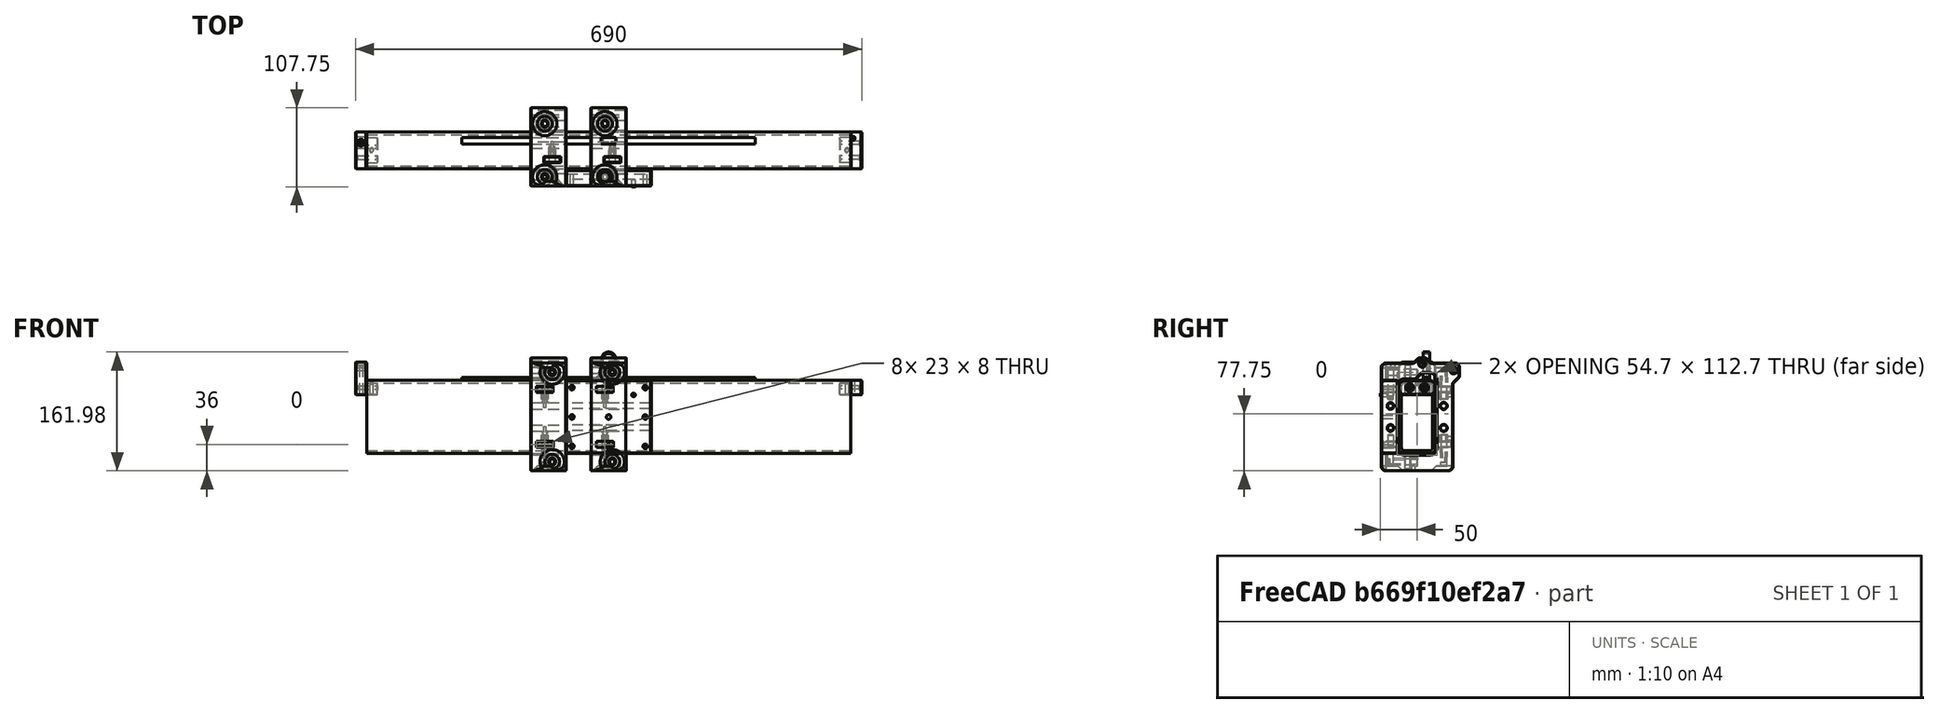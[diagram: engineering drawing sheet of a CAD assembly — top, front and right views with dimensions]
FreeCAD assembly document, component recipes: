
FREECAD ASSEMBLY — COMPONENT RECIPES ("Fabricatable-Axis-6.0")

This assembly document has 12 components, labeled P0..P11 below (a component is one placed body or linked part). 11 of them carry a construction recipe — the FreeCAD feature program that regenerates the part from scratch, quoted from this document or its linked companion documents; the rest are supplied as boundary geometry only. No exploded tour is included for this assembly.
COMPONENT P0 — recipe-attached ("Body - hole maker non adjustable", modeled in this document).
Construction recipe (the document's own serialized feature program — sketch geometry with constraints, then the solid features built on it; lengths are millimeters unless a unit is written):

FEATURE [Sketcher::SketchObject] Sketch005
  ArcFitTolerance = 1e-06
  AttachmentSupport = -> [XY_Plane008]
  FullyConstrained = true
  MakeInternals = false
  MapMode = 5
  expr: Constraints[11] = -VarSet.Bearing_od / 2 - VarSet.Carriage_to_bearing_top_clearance
  expr: Constraints[31] = VarSet.Bearing_slot_width_margin + VarSet.Bearing_od + 2 mm
  expr: Constraints[32] = -VarSet.Bearing_od / 2 - VarSet.Carriage_to_bearing_top_clearance + 1 mm
  expr: Constraints[33] = -VarSet.Bearing_od / 2 - VarSet.Carriage_to_bearing_top_clearance + 3 mm
  expr: Constraints[8] = VarSet.Bearing_slot_width_margin + VarSet.Bearing_od
  expr: Constraints[9] = VarSet.Bearing_od / 2
  sketch-geometry (13):
    g0: LineSegment StartX=11.5 StartY=-12.5 StartZ=0 EndX=11.5 EndY=11 EndZ=0
    g1: LineSegment StartX=11.5 StartY=11 StartZ=0 EndX=-11.5 EndY=11 EndZ=0
    g2: LineSegment StartX=-11.5 StartY=11 StartZ=0 EndX=-11.5 EndY=-12.5 EndZ=0
    g3: LineSegment StartX=-11.5 StartY=-12.5 StartZ=0 EndX=11.5 EndY=-12.5 EndZ=0
    g4: GeomPoint [constr] X=0 Y=0 Z=0
    g5: LineSegment StartX=11.5 StartY=-11.5 StartZ=0 EndX=12.5 EndY=-11.5 EndZ=0
    g6: LineSegment StartX=12.5 StartY=-11.5 StartZ=0 EndX=12.5 EndY=-9.5 EndZ=0
    g7: LineSegment StartX=12.5 StartY=-9.5 StartZ=0 EndX=11.5 EndY=-9.5 EndZ=0
    g8: LineSegment StartX=11.5 StartY=-9.5 StartZ=0 EndX=11.5 EndY=-11.5 EndZ=0
    g9: LineSegment StartX=-11.5 StartY=-9.5 StartZ=0 EndX=-12.5 EndY=-9.5 EndZ=0
    g10: LineSegment StartX=-12.5 StartY=-9.5 StartZ=0 EndX=-12.5 EndY=-11.5 EndZ=0
    g11: LineSegment StartX=-12.5 StartY=-11.5 StartZ=0 EndX=-11.5 EndY=-11.5 EndZ=0
    g12: LineSegment StartX=-11.5 StartY=-11.5 StartZ=0 EndX=-11.5 EndY=-9.5 EndZ=0
  constraints (34):
    c: Coincident(g0,g1)
    c: Coincident(g1,g2)
    c: Coincident(g2,g3)
    c: Coincident(g3,g0)
    c: Vertical(g0)
    c: Vertical(g2)
    c: Horizontal(g1)
    c: Coincident(g4,g-1)
    c: Distance(g3) = 23
    c: DistanceY(g-1,g0) = 11
    c: Symmetric(g0,g2,g-2)
    c: DistanceY(g-1,g0) = -12.5
    c: Coincident(g5,g6)
    c: Coincident(g6,g7)
    c: Coincident(g7,g8)
    c: Coincident(g8,g5)
    c: Horizontal(g5)
    c: Horizontal(g7)
    c: Vertical(g6)
    c: Vertical(g8)
    c: PointOnObject(g5,g0)
    c: Coincident(g9,g10)
    c: Coincident(g10,g11)
    c: Coincident(g11,g12)
    c: Coincident(g12,g9)
    c: Horizontal(g9)
    c: Horizontal(g11)
    c: Vertical(g10)
    c: Vertical(g12)
    c: Symmetric(g9,g7,g-2)
    c: Symmetric(g10,g5,g-2)
    c: Distance(g5,g10) = 25
    c: DistanceY(g-1,g5) = -11.5
    c: DistanceY(g-1,g6) = -9.5
FEATURE [PartDesign::Pad] Pad004
  Direction = (0,0,1)
  Length = 8
  Length2 = 10
  Midplane = true
  Profile = -> Sketch005
  ReferenceAxis = -> Sketch005 [N_Axis]
  Refine = true
  Suppressed = false
  Type = 0
  expr: Length = VarSet.Bearing_width + VarSet.Bearing_slot_width_margin
FEATURE [Sketcher::SketchObject] Sketch007
  ArcFitTolerance = 1e-06
  AttachmentOffset = pos=(0,0,4) rot=(0,0,1;0rad)
  AttachmentSupport = -> [XY_Plane008]
  FullyConstrained = true
  MakeInternals = false
  MapMode = 5
  Placement = pos=(0,0,4) rot=(0,0,1;0rad)
  expr: .AttachmentOffset.Base.z = Pad004.Length / 2
  expr: Constraints[1] = VarSet.Bearing_od / 1.8
  sketch-geometry (1):
    g0: Circle CenterX=0 CenterY=0 CenterZ=0 NormalX=0 NormalY=0 NormalZ=1 AngleXU=0 Radius=6.11111
  constraints (2):
    c: Coincident(g0,g-1)
    c: Diameter(g0) = 12.2222
FEATURE [PartDesign::Pocket] Pocket001
  BaseFeature = -> Pad004
  Direction = (0,0,-1)
  Length = 0.36
  Length2 = 5
  Profile = -> Sketch007
  ReferenceAxis = -> Sketch007 [N_Axis]
  Refine = true
  Suppressed = false
  Type = 0
  expr: Length = VarSet.Bearing_washer_protrusion
FEATURE [PartDesign::LinearPattern] LinearPattern
  BaseFeature = -> Pocket001
  Direction = -> Z_Axis008
  Length = 7.64
  Mode = 0
  Occurrences = 2
  Offset = 7.64
  Originals = -> [Pocket001]
  Refine = true
  Reversed = true
  Suppressed = false
  TransformMode = 0
  expr: Length = Pad004.Length - Pocket001.Length
FEATURE [Sketcher::SketchObject] Sketch008
  ArcFitTolerance = 1e-06
  AttachmentSupport = -> [XY_Plane008]
  FullyConstrained = true
  MakeInternals = false
  MapMode = 5
  expr: Constraints[1] = VarSet.Bearing_axle_screw_selftap_diameter
  sketch-geometry (1):
    g0: Circle CenterX=0 CenterY=0 CenterZ=0 NormalX=0 NormalY=0 NormalZ=1 AngleXU=0 Radius=3.85
  constraints (2):
    c: Coincident(g0,g-1)
    c: Diameter(g0) = 7.7
FEATURE [PartDesign::Pad] Pad005
  BaseFeature = -> LinearPattern
  Direction = (0,0,1)
  Length = 29.5
  Length2 = 10
  Profile = -> Sketch008
  ReferenceAxis = -> Sketch008 [N_Axis]
  Refine = true
  Suppressed = false
  Type = 0
  expr: Length = VarSet.Bearing_width / 2 + VarSet.Bearing_distance_from_fillet + VarSet.Tube_fillet_radius + VarSet.Bearing_od + VarSet.Carriage_to_bearing_top_clearance - VarSet.Bearing_axle_screw_head_pocket_depth
FEATURE [PartDesign::Pad] Pad006
  BaseFeature = -> Pad005
  Direction = (0,0,1)
  Length = 13.5
  Length2 = 10
  Profile = -> Sketch008
  ReferenceAxis = -> Sketch008 [N_Axis]
  Refine = true
  Reversed = true
  Suppressed = false
  Type = 0
  expr: Length = VarSet.Bearing_axle_screw_length + 3 mm - Pad005.Length
FEATURE [Sketcher::SketchObject] Sketch009
  ArcFitTolerance = 1e-06
  AttachmentSupport = -> [Pad006]
  FullyConstrained = true
  MakeInternals = false
  MapMode = 5
  Placement = pos=(0,0,29.5) rot=(0,0,1;0rad)
  expr: Constraints[1] = VarSet.Bearing_axle_screw_head_pocket_diamter
  sketch-geometry (1):
    g0: Circle CenterX=0 CenterY=0 CenterZ=0 NormalX=0 NormalY=0 NormalZ=1 AngleXU=0 Radius=10
  constraints (2):
    c: Coincident(g0,g-1)
    c: Diameter(g0) = 20
FEATURE [PartDesign::Pad] Pad007
  BaseFeature = -> Pad006
  Direction = (0,0,1)
  Length = 6.5
  Length2 = 10
  Profile = -> Sketch009
  ReferenceAxis = -> Sketch009 [N_Axis]
  Refine = true
  Suppressed = false
  TaperAngle = 45
  Type = 0
  expr: Length = VarSet.Bearing_axle_screw_head_pocket_depth
FEATURE [PartDesign::Chamfer] Chamfer002
  Angle = 45
  Base = -> Pad007 [Edge46,Edge48]
  BaseFeature = -> Pad007
  ChamferType = 0
  FlipDirection = false
  Refine = true
  Size = 0.8
  Size2 = 1
  SupportTransform = false
  Suppressed = false
  UseAllEdges = false
FEATURE [PartDesign::Chamfer] Chamfer003
  Angle = 45
  Base = -> Chamfer002 [Edge51,Edge3]
  BaseFeature = -> Chamfer002
  ChamferType = 0
  FlipDirection = false
  Refine = true
  Size = 0.3
  Size2 = 1
  SupportTransform = false
  Suppressed = false
  UseAllEdges = false
FEATURE [PartDesign::Body] Body004  label="Body - hole maker non adjustable"
  AllowCompound = false
  Group = -> [Sketch005,Pad004,Sketch007,Pocket001,LinearPattern,Sketch008,Pad005,Pad006,Sketch009,Pad007,Chamfer002,Chamfer003]
  Origin = -> Origin008
  Tip = -> Chamfer003
COMPONENT P1 — recipe-attached ("Body for boolean - hole maker adjustable", modeled in this document).
Construction recipe (the document's own serialized feature program — sketch geometry with constraints, then the solid features built on it; lengths are millimeters unless a unit is written):

FEATURE [PartDesign::FeatureBase] Clone007
  BaseFeature = -> LinearPattern
  Suppressed = false
FEATURE [PartDesign::Body] Body005  label="Body for boolean - hole maker adjustable"
  AllowCompound = false
  Group = -> [Clone007]
  Origin = -> Origin009
  Tip = -> Clone007
COMPONENT P2 — recipe-attached ("Body for boolean - rotation hole", modeled in this document).
Construction recipe (the document's own serialized feature program — sketch geometry with constraints, then the solid features built on it; lengths are millimeters unless a unit is written):

FEATURE [Sketcher::SketchObject] Sketch013
  ArcFitTolerance = 1e-06
  AttachmentSupport = -> [YZ_Plane011]
  FullyConstrained = true
  MakeInternals = false
  MapMode = 5
  Placement = pos=(0,0,0) rot=(0.57735,0.57735,0.57735;2.0944rad)
  expr: .Constraints.z = Pad005.Length - VarSet.Bearing_axel_screw_oval_hole_depth
  expr: Constraints[12] = VarSet.Bearing_axle_screw_diameter_loose_diamter + VarSet.Tuning_range_bearing
  expr: Constraints[7] = -Pad006.Length
  expr: Constraints[8] = VarSet.Bearing_axle_screw_diameter_loose_diamter
  sketch-geometry (5):
    g0: LineSegment StartX=-4.25 StartY=24.5 StartZ=0 EndX=-5.80102 EndY=-13.5 EndZ=0
    g1: LineSegment StartX=-5.80102 StartY=-13.5 StartZ=0 EndX=5.80102 EndY=-13.5 EndZ=0
    g2: LineSegment StartX=5.80102 StartY=-13.5 StartZ=0 EndX=4.25 EndY=24.5 EndZ=0
    g3: LineSegment StartX=4.25 StartY=24.5 StartZ=0 EndX=-4.25 EndY=24.5 EndZ=0
    g4: LineSegment [constr] StartX=-5.25 StartY=0 StartZ=0 EndX=5.25 EndY=0 EndZ=0
  constraints (14):
    c: Coincident(g0,g1)
    c: Coincident(g1,g2)
    c: Coincident(g2,g3)
    c: Coincident(g3,g0)
    c: Symmetric(g2,g0,g-2)
    c: Symmetric(g0,g1,g-2)
    c: DistanceY(g-1,g2) = 24.5  'z'
    c: DistanceY(g-1,g1) = -13.5
    c: Distance(g3) = 8.5
    c: Distance(g1) = 11.602
    c: PointOnObject(g4,g-1)
    c: Symmetric(g4,g4,g-2)
    c: Distance(g4) = 10.5
    c: PointOnObject(g4,g0)
FEATURE [PartDesign::Pad] Pad008
  Direction = (1,0,0)
  Length = 8.5
  Length2 = 10
  Midplane = true
  Placement = pos=(0,0,0) rot=(1,1,1;2.0944rad)
  Profile = -> Sketch013
  ReferenceAxis = -> Sketch013 [N_Axis]
  Refine = true
  Suppressed = false
  Type = 0
  expr: Length = VarSet.Bearing_axle_screw_diameter_loose_diamter
FEATURE [PartDesign::Chamfer] Chamfer004
  Angle = 45
  Base = -> Pad008 [Edge4,Edge3,Edge10,Edge9]
  BaseFeature = -> Pad008
  ChamferType = 0
  FlipDirection = false
  Placement = pos=(0,0,0) rot=(1,1,1;2.0944rad)
  Refine = true
  Size = 2.42857
  Size2 = 1
  SupportTransform = false
  Suppressed = false
  UseAllEdges = false
  expr: Size = VarSet.Bearing_axle_screw_diameter_loose_diamter / 3.5
FEATURE [PartDesign::Chamfer] Chamfer005
  Angle = 45
  Base = -> Chamfer004 [Face5]
  BaseFeature = -> Chamfer004
  ChamferType = 0
  FlipDirection = false
  Placement = pos=(0,0,0) rot=(1,1,1;2.0944rad)
  Refine = true
  Size = 0.8
  Size2 = 1
  SupportTransform = false
  Suppressed = false
  UseAllEdges = false
FEATURE [Sketcher::SketchObject] Sketch014
  ArcFitTolerance = 1e-06
  AttachmentOffset = pos=(0,0,24.5) rot=(0,0,1;0rad)
  AttachmentSupport = -> [XY_Plane011]
  FullyConstrained = false
  MakeInternals = false
  MapMode = 5
  Placement = pos=(0,0,24.5) rot=(0,0,1;0rad)
  expr: .AttachmentOffset.Base.z = Sketch013.Constraints.z
  expr: Constraints[5] = VarSet.Bearing_axle_screw_diameter
  expr: Constraints[6] = VarSet.Bearing_axle_screw_diameter_oval_selftap_diameter
  sketch-geometry (5):
    g0: Ellipse CenterX=0 CenterY=0 CenterZ=0 NormalX=0 NormalY=0 NormalZ=1 MajorRadius=4 MinorRadius=3.75 AngleXU=-1.5708
    g1: LineSegment [constr] StartX=1e-16 StartY=-4 StartZ=0 EndX=-1e-16 EndY=4 EndZ=0
    g2: LineSegment [constr] StartX=3.75 StartY=1e-16 StartZ=0 EndX=-3.75 EndY=-1e-16 EndZ=0
    g3: GeomPoint [constr] X=2e-16 Y=-1.39194 Z=0
    g4: GeomPoint [constr] X=0 Y=1.39194 Z=0
  constraints (4):
    c: InternalAlignment(g1-g4 -> g0) x4
    c: Coincident(g0,g-1)
    c: Distance(g1,g1) = 8
    c: Distance(g2,g2) = 7.5
FEATURE [PartDesign::Pad] Pad009
  BaseFeature = -> Chamfer005
  Direction = (0,0,1)
  Length = 5
  Length2 = 10
  Placement = pos=(0,0,0) rot=(1,1,1;2.0944rad)
  Profile = -> Sketch014
  ReferenceAxis = -> Sketch014 [N_Axis]
  Refine = true
  Suppressed = false
  Type = 0
  expr: Length = VarSet.Bearing_axel_screw_oval_hole_depth
FEATURE [Sketcher::SketchObject] Sketch015
  ArcFitTolerance = 1e-06
  AttachmentOffset = pos=(0,0,29.5) rot=(0,0,1;0rad)
  AttachmentSupport = -> [XY_Plane011]
  FullyConstrained = true
  MakeInternals = false
  MapMode = 5
  Placement = pos=(0,0,29.5) rot=(0,0,1;0rad)
  expr: .AttachmentOffset.Base.z = Sketch013.Constraints.z + VarSet.Bearing_axel_screw_oval_hole_depth
  expr: Constraints[1] = VarSet.Bearing_axle_screw_head_pocket_diamter
  sketch-geometry (1):
    g0: Circle CenterX=0 CenterY=0 CenterZ=0 NormalX=0 NormalY=0 NormalZ=1 AngleXU=0 Radius=10
  constraints (2):
    c: Coincident(g0,g-1)
    c: Diameter(g0) = 20
FEATURE [PartDesign::Pad] Pad010
  BaseFeature = -> Pad009
  Direction = (0,0,1)
  Length = 32.5
  Length2 = 10
  Placement = pos=(0,0,0) rot=(1,1,1;2.0944rad)
  Profile = -> Sketch015
  ReferenceAxis = -> Sketch015 [N_Axis]
  Refine = true
  Suppressed = false
  TaperAngle = 45
  Type = 0
  expr: Length = VarSet.Bearing_axle_screw_head_pocket_depth * 5
FEATURE [Sketcher::SketchObject] Sketch016
  ArcFitTolerance = 1e-06
  AttachmentSupport = -> [XZ_Plane011]
  FullyConstrained = true
  MakeInternals = false
  MapMode = 5
  Placement = pos=(0,0,0) rot=(1,0,0;1.5708rad)
  expr: .Constraints.z = -VarSet.Bearing_width / 2 - VarSet.Bearing_slot_width_margin / 2 - VarSet.Bearing_tuning_screw_selftap_diameter / 2 - 1.8 mm
  expr: Constraints[1] = VarSet.Bearing_tuning_screw_selftap_diameter
  sketch-geometry (1):
    g0: Circle CenterX=0 CenterY=-8.1 CenterZ=0 NormalX=0 NormalY=0 NormalZ=1 AngleXU=0 Radius=2.3
  constraints (3):
    c: PointOnObject(g0,g-2)
    c: Diameter(g0) = 4.6
    c: DistanceY(g-1,g0) = -8.1  'z'
FEATURE [PartDesign::Pad] Pad011
  BaseFeature = -> Pad010
  Direction = (0,-1,2e-16)
  Length = 11.5
  Length2 = 10
  Placement = pos=(0,0,0) rot=(1,1,1;2.0944rad)
  Profile = -> Sketch016
  ReferenceAxis = -> Sketch016 [N_Axis]
  Refine = true
  Suppressed = false
  Type = 0
  expr: Length = VarSet.Bearing_od / 2 + VarSet.Carriage_to_bearing_top_clearance - 1 mm
FEATURE [Sketcher::SketchObject] Sketch017
  ArcFitTolerance = 1e-06
  AttachmentOffset = pos=(0,0,11.5) rot=(0,0,1;0rad)
  AttachmentSupport = -> [XZ_Plane011]
  FullyConstrained = true
  MakeInternals = false
  MapMode = 5
  Placement = pos=(0,-11.5,2.6e-15) rot=(1,0,0;1.5708rad)
  expr: .AttachmentOffset.Base.z = VarSet.Bearing_od / 2 + VarSet.Carriage_to_bearing_top_clearance - 1 mm
  expr: Constraints[0] = VarSet.Bearing_tuning_screw_selftap_diameter
  expr: Constraints[1] = Sketch016.Constraints.z
  sketch-geometry (1):
    g0: Circle CenterX=0 CenterY=-8.1 CenterZ=0 NormalX=0 NormalY=0 NormalZ=1 AngleXU=0 Radius=2.3
  constraints (3):
    c: Diameter(g0) = 4.6
    c: DistanceY(g-1,g0) = -8.1
    c: PointOnObject(g0,g-2)
FEATURE [PartDesign::Pad] Pad012
  BaseFeature = -> Pad011
  Direction = (0,-1,2e-16)
  Length = 1
  Length2 = 10
  Placement = pos=(0,0,0) rot=(1,1,1;2.0944rad)
  Profile = -> Sketch017
  ReferenceAxis = -> Sketch017 [N_Axis]
  Refine = true
  Suppressed = false
  TaperAngle = 45
  Type = 0
FEATURE [PartDesign::Chamfer] Chamfer006
  Angle = 45
  Base = -> Pad012 [Edge44]
  BaseFeature = -> Pad012
  ChamferType = 0
  FlipDirection = false
  Placement = pos=(0,0,0) rot=(1,1,1;2.0944rad)
  Refine = true
  Size = 0.8
  Size2 = 1
  SupportTransform = false
  Suppressed = false
  UseAllEdges = false
FEATURE [PartDesign::Body] Body007  label="Body for boolean - rotation hole"
  AllowCompound = false
  Group = -> [Sketch013,Pad008,Chamfer004,Chamfer005,Sketch014,Pad009,Sketch015,Pad010,Sketch016,Pad011,Sketch017,Pad012,Chamfer006]
  Origin = -> Origin011
  Tip = -> Chamfer006
COMPONENT P3 — recipe-attached ("Belt", modeled in this document).
Construction recipe (the document's own serialized feature program — sketch geometry with constraints, then the solid features built on it; lengths are millimeters unless a unit is written):

FEATURE [Sketcher::SketchObject] Sketch018
  ArcFitTolerance = 1e-06
  AttachmentSupport = -> [XZ_Plane012]
  FullyConstrained = false
  MakeInternals = false
  MapMode = 5
  Placement = pos=(0,0,0) rot=(1,0,0;1.5708rad)
  expr: Constraints[31] = 16
  sketch-geometry (16):
    g0: LineSegment StartX=-200 StartY=0 StartZ=0 EndX=-21 EndY=0 EndZ=0
    g1: LineSegment StartX=21 StartY=0 StartZ=0 EndX=200 EndY=0 EndZ=0
    g2: ArcOfCircle CenterX=-1e-16 CenterY=26.9798 CenterZ=0 NormalX=0 NormalY=0 NormalZ=1 AngleXU=0 Radius=8 StartAngle=1e-16 EndAngle=3.14159
    g3: ArcOfCircle CenterX=-1e-16 CenterY=26.9798 CenterZ=0 NormalX=0 NormalY=0 NormalZ=1 AngleXU=0 Radius=10 StartAngle=0 EndAngle=3.14159
    g4: ArcOfCircle CenterX=-21 CenterY=13 CenterZ=0 NormalX=0 NormalY=0 NormalZ=1 AngleXU=0 Radius=13 StartAngle=4.71239 EndAngle=6.28319
    g5: ArcOfCircle CenterX=21 CenterY=13 CenterZ=0 NormalX=0 NormalY=0 NormalZ=1 AngleXU=0 Radius=13 StartAngle=3.14159 EndAngle=4.71239
    g6: ArcOfCircle CenterX=21 CenterY=13 CenterZ=0 NormalX=0 NormalY=0 NormalZ=1 AngleXU=0 Radius=11 StartAngle=3.14159 EndAngle=4.71239
    g7: ArcOfCircle CenterX=-21 CenterY=13 CenterZ=0 NormalX=0 NormalY=0 NormalZ=1 AngleXU=0 Radius=11 StartAngle=4.71239 EndAngle=6.28319
    g8: LineSegment StartX=-200 StartY=0 StartZ=0 EndX=-200 EndY=2 EndZ=0
    g9: LineSegment StartX=-200 StartY=2 StartZ=0 EndX=-21 EndY=2 EndZ=0
    g10: LineSegment StartX=200 StartY=0 StartZ=0 EndX=200 EndY=2 EndZ=0
    g11: LineSegment StartX=200 StartY=2 StartZ=0 EndX=21 EndY=2 EndZ=0
    g12: LineSegment StartX=-10 StartY=26.9798 StartZ=0 EndX=-10 EndY=13 EndZ=0
    g13: LineSegment StartX=-8 StartY=26.9798 StartZ=0 EndX=-8 EndY=13 EndZ=0
    g14: LineSegment StartX=8 StartY=26.9798 StartZ=0 EndX=8 EndY=13 EndZ=0
    g15: LineSegment StartX=10 StartY=26.9798 StartZ=0 EndX=10 EndY=13 EndZ=0
  constraints (36):
    c: PointOnObject(g0,g-1)
    c: PointOnObject(g0,g-1)
    c: PointOnObject(g1,g-1)
    c: Coincident(g3,g2)
    c: Coincident(g6,g5)
    c: Coincident(g7,g4)
    c: Coincident(g0,g8)
    c: Vertical(g8)
    c: Coincident(g8,g9)
    c: Horizontal(g9)
    c: Coincident(g1,g10)
    c: Vertical(g10)
    c: Coincident(g10,g11)
    c: Horizontal(g11)
    c: Tangent(g1,g5) = -1.5708
    c: Tangent(g6,g11) = 1.5708
    c: Tangent(g5,g14) = -1.5708
    c: Tangent(g15,g6) = -1.5708
    c: Tangent(g15,g3) = 1.5708
    c: Tangent(g14,g2) = 1.5708
    c: Tangent(g4,g0) = -1.5708
    c: Tangent(g7,g9) = -1.5708
    c: Tangent(g7,g12) = 1.5708
    c: Tangent(g4,g13) = 1.5708
    c: Tangent(g13,g2) = -1.5708
    c: Tangent(g12,g3) = -1.5708
    c: Parallel(g12,g13)
    c: Parallel(g14,g15)
    c: Symmetric(g2,g2,g-2)
    c: Vertical(g12)
    c: Distance(g8) = 2
    c: Diameter(g2) = 16
    c: Equal(g7,g6)
    c: Diameter(g7) = 22
    c: Symmetric(g0,g1,g-2)
    c: Distance(g0,g1) = 400
FEATURE [PartDesign::Pad] Pad013
  Direction = (0,-1,2e-16)
  Length = 9
  Length2 = 10
  Placement = pos=(0,0,0) rot=(1,0,0;1.5708rad)
  Profile = -> Sketch018
  ReferenceAxis = -> Sketch018 [N_Axis]
  Refine = true
  Suppressed = false
  Type = 0
FEATURE [PartDesign::Body] Body008  label="Belt"
  AllowCompound = false
  Group = -> [Sketch018,Pad013]
  Origin = -> Origin012
  Placement = pos=(0,17.25,51.5) rot=(0,0,1;0rad)
  Tip = -> Pad013
  expr: .Placement.Base.y = VarSet.Tube_width / 2 - VarSet.Tube_fillet_radius
  expr: .Placement.Base.z = VarSet.Tube_height / 2 + 1.5 mm
COMPONENT P4 — recipe-attached ("Tuning arrow", modeled in this document).
Construction recipe (the document's own serialized feature program — sketch geometry with constraints, then the solid features built on it; lengths are millimeters unless a unit is written):

FEATURE [Sketcher::SketchObject] Sketch019
  ArcFitTolerance = 1e-06
  AttachmentOffset = pos=(0,-12.7,12.5) rot=(0,0,1;0rad)
  AttachmentSupport = -> [XZ_Plane013]
  FullyConstrained = true
  MakeInternals = false
  MapMode = 5
  Placement = pos=(0,-12.5,-12.7) rot=(1,0,0;1.5708rad)
  expr: .AttachmentOffset.Base.y = Sketch016.Constraints.z - VarSet.Bearing_tuning_screw_selftap_diameter
  expr: .AttachmentOffset.Base.z = VarSet.Bearing_od / 2 + VarSet.Carriage_to_bearing_top_clearance
  sketch-geometry (10):
    g0: LineSegment StartX=-1.25 StartY=-12 StartZ=0 EndX=1.25 EndY=-12 EndZ=0
    g1: LineSegment StartX=1.25 StartY=-12 StartZ=0 EndX=1.25 EndY=-3.82843 EndZ=0
    g2: LineSegment StartX=1.25 StartY=-3.82843 StartZ=0 EndX=3.5 EndY=-6.07843 EndZ=0
    g3: LineSegment StartX=3.5 StartY=-6.07843 StartZ=0 EndX=3.5 EndY=-3.25 EndZ=0
    g4: LineSegment StartX=3.5 StartY=-3.25 StartZ=0 EndX=0.25 EndY=-4e-16 EndZ=0
    g5: LineSegment StartX=0.25 StartY=-4e-16 StartZ=0 EndX=-0.25 EndY=0 EndZ=0
    g6: LineSegment StartX=-0.25 StartY=0 StartZ=0 EndX=-3.5 EndY=-3.25 EndZ=0
    g7: LineSegment StartX=-3.5 StartY=-3.25 StartZ=0 EndX=-3.5 EndY=-6.07843 EndZ=0
    g8: LineSegment StartX=-3.5 StartY=-6.07843 StartZ=0 EndX=-1.25 EndY=-3.82843 EndZ=0
    g9: LineSegment StartX=-1.25 StartY=-3.82843 StartZ=0 EndX=-1.25 EndY=-12 EndZ=0
  constraints (26):
    c: Horizontal(g0)
    c: Coincident(g0,g1)
    c: Vertical(g1)
    c: Coincident(g1,g2)
    c: Coincident(g2,g3)
    c: Vertical(g3)
    c: Coincident(g3,g4)
    c: Coincident(g4,g5)
    c: Coincident(g5,g6)
    c: Coincident(g6,g7)
    c: Coincident(g7,g8)
    c: Coincident(g8,g9)
    c: Coincident(g9,g0)
    c: Vertical(g9)
    c: Symmetric(g5,g4,g-2)
    c: Symmetric(g6,g3,g-2)
    c: Symmetric(g8,g1,g-2)
    c: Symmetric(g7,g2,g-2)
    c: Distance(g5) = 0.5
    c: Parallel(g8,g6)
    c: Distance(g8,g6) = 2
    c: Distance(g0) = 2.5
    c: Angle(g8,g9) = 0.785398
    c: Distance(g7,g2) = 7
    c: PointOnObject(g4,g-1)
    c: DistanceY(g-1,g0) = -12
FEATURE [PartDesign::Pad] Pad014
  Direction = (0,-1,2e-16)
  Length = 0.5
  Length2 = 10
  Placement = pos=(0,0,0) rot=(1,0,0;1.5708rad)
  Profile = -> Sketch019
  ReferenceAxis = -> Sketch019 [N_Axis]
  Refine = true
  Reversed = true
  Suppressed = false
  Type = 0
FEATURE [PartDesign::Body] Body009  label="Tuning arrow"
  AllowCompound = false
  Group = -> [Sketch019,Pad014]
  Origin = -> Origin013
  Tip = -> Pad014
COMPONENT P5 — recipe-attached ("Connector for bearing rings", modeled in this document).
Construction recipe (the document's own serialized feature program — sketch geometry with constraints, then the solid features built on it; lengths are millimeters unless a unit is written):

FEATURE [Sketcher::SketchObject] Sketch023
  ArcFitTolerance = 1e-06
  AttachmentSupport = -> [YZ_Plane016]
  FullyConstrained = true
  MakeInternals = false
  MapMode = 5
  Placement = pos=(0,0,0) rot=(0.57735,0.57735,0.57735;2.0944rad)
  expr: Constraints[10] = -VarSet.Tube_width / 2 - VarSet.Carriage_to_tube_clearance
  expr: Constraints[12] = Sketch022.Constraints.holespacing
  expr: Constraints[13] = -Sketch022.Constraints.holelocation
  expr: Constraints[15] = VarSet.Bearing_axle_screw_selftap_diameter
  expr: Constraints[8] = VarSet.Tube_height
  expr: Constraints[9] = -VarSet.Tube_width / 2 - VarSet.Bearing_od - VarSet.Carriage_to_bearing_top_clearance
  sketch-geometry (6):
    g0: LineSegment StartX=-48.75 StartY=50 StartZ=0 EndX=-48.75 EndY=-50 EndZ=0
    g1: LineSegment StartX=-48.75 StartY=-50 StartZ=0 EndX=-26.75 EndY=-50 EndZ=0
    g2: LineSegment StartX=-26.75 StartY=-50 StartZ=0 EndX=-26.75 EndY=50 EndZ=0
    g3: LineSegment StartX=-26.75 StartY=50 StartZ=0 EndX=-48.75 EndY=50 EndZ=0
    g4: Circle CenterX=-36.25 CenterY=15 CenterZ=0 NormalX=0 NormalY=0 NormalZ=1 AngleXU=0 Radius=3.85
    g5: Circle CenterX=-36.25 CenterY=-15 CenterZ=0 NormalX=0 NormalY=0 NormalZ=1 AngleXU=0 Radius=3.85
  constraints (16):
    c: Coincident(g0,g1)
    c: Coincident(g1,g2)
    c: Coincident(g2,g3)
    c: Coincident(g3,g0)
    c: Vertical(g2)
    c: Horizontal(g1)
    c: Horizontal(g3)
    c: Symmetric(g0,g0,g-1)
    c: Distance(g0) = 100
    c: DistanceX(g-2,g0) = -48.75
    c: DistanceX(g-2,g2) = -26.75
    c: Symmetric(g4,g5,g-1)
    c: Distance(g5,g4) = 30
    c: DistanceX(g-2,g4) = -36.25
    c: Equal(g5,g4)
    c: Diameter(g5) = 7.7
FEATURE [PartDesign::Pad] Pad016
  Direction = (1,0,0)
  Length = 116
  Length2 = 10
  Midplane = true
  Placement = pos=(0,0,0) rot=(1,1,1;2.0944rad)
  Profile = -> Sketch023
  ReferenceAxis = -> Sketch023 [N_Axis]
  Refine = true
  Suppressed = false
  Type = 0
  expr: Length = <<Bearing ring 1>>.Placement.Base.x * 2 - Pad002.Length
FEATURE [Sketcher::SketchObject] Sketch024
  ArcFitTolerance = 1e-06
  AttachmentSupport = -> [Pad016]
  FullyConstrained = false
  MakeInternals = false
  MapMode = 5
  Placement = pos=(-1.07e-14,-48.75,0) rot=(0.57735,0.57735,-0.57735;2.0944rad)
  sketch-geometry (9):
    g0: Circle CenterX=-40 CenterY=-50 CenterZ=0 NormalX=0 NormalY=0 NormalZ=1 AngleXU=0 Radius=3.64196
    g1: Circle CenterX=-40 CenterY=0 CenterZ=0 NormalX=0 NormalY=0 NormalZ=1 AngleXU=0 Radius=6.80044
    g2: Circle CenterX=-40 CenterY=50 CenterZ=0 NormalX=0 NormalY=0 NormalZ=1 AngleXU=0 Radius=7.67268
    g3: Circle CenterX=40 CenterY=50 CenterZ=0 NormalX=0 NormalY=0 NormalZ=1 AngleXU=0 Radius=3.2152
    g4: Circle CenterX=40 CenterY=0 CenterZ=0 NormalX=0 NormalY=0 NormalZ=1 AngleXU=0 Radius=11.4747
    g5: Circle CenterX=40 CenterY=-50 CenterZ=0 NormalX=0 NormalY=0 NormalZ=1 AngleXU=0 Radius=5.49329
    g6: Circle CenterX=0 CenterY=-50 CenterZ=0 NormalX=0 NormalY=0 NormalZ=1 AngleXU=0 Radius=9.23188
    g7: Circle CenterX=0 CenterY=0 CenterZ=0 NormalX=0 NormalY=0 NormalZ=1 AngleXU=0 Radius=8.68214
    g8: Circle CenterX=0 CenterY=50 CenterZ=0 NormalX=0 NormalY=0 NormalZ=1 AngleXU=0 Radius=6.29187
  constraints (14):
    c: PointOnObject(g1,g-1)
    c: PointOnObject(g4,g-1)
    c: PointOnObject(g6,g-2)
    c: Coincident(g7,g-1)
    c: PointOnObject(g8,g-2)
    c: Vertical(g0,g1)
    c: Vertical(g5,g4)
    c: Symmetric(g5,g3,g-1)
    c: Symmetric(g2,g0,g-1)
    c: Symmetric(g2,g3,g-2)
    c: Horizontal(g8,g3)
    c: Horizontal(g6,g5)
    c: Distance(g5,g0) = 80
    c: Distance(g0,g2) = 100
FEATURE [PartDesign::Hole] Hole
  BaseFeature = -> Pad016
  CustomThreadClearance = 0
  Depth = 316.338
  DepthType = 1
  Diameter = 4.6
  DrillForDepth = false
  DrillPoint = 1
  DrillPointAngle = 118
  HoleCutCountersinkAngle = 90
  HoleCutCustomValues = false
  HoleCutDepth = 0
  HoleCutDiameter = 6.1
  HoleCutType = 0
  ModelThread = false
  Placement = pos=(0,0,0) rot=(1,1,1;2.0944rad)
  Profile = -> Sketch024
  Refine = true
  Suppressed = false
  Tapered = false
  TaperedAngle = 90
  ThreadClass = 0
  ThreadDepth = 316.338
  ThreadDepthType = 0
  ThreadDirection = 0
  ThreadFit = 0
  ThreadSize = 0
  ThreadType = 0
  Threaded = false
  UseCustomThreadClearance = false
  expr: Diameter = VarSet.Bearing_tuning_screw_selftap_diameter
FEATURE [PartDesign::Chamfer] Chamfer009
  Angle = 45
  Base = -> Hole [Face1,Face4,Face3,Face15]
  BaseFeature = -> Hole
  ChamferType = 0
  FlipDirection = false
  Placement = pos=(0,0,0) rot=(1,1,1;2.0944rad)
  Refine = true
  Size = 0.8
  Size2 = 1
  SupportTransform = false
  Suppressed = false
  UseAllEdges = false
FEATURE [PartDesign::Body] Body012  label="Connector for bearing rings"
  AllowCompound = false
  Group = -> [Sketch023,Pad016,Sketch024,Hole,Chamfer009]
  Origin = -> Origin016
  Tip = -> Chamfer009
COMPONENT P6 — recipe-attached ("Chain lock - non-adjustable", modeled in this document).
Construction recipe (the document's own serialized feature program — sketch geometry with constraints, then the solid features built on it; lengths are millimeters unless a unit is written):

FEATURE [Sketcher::SketchObject] Sketch025
  ArcFitTolerance = 1e-06
  AttachmentSupport = -> [YZ_Plane017]
  FullyConstrained = true
  MakeInternals = false
  MapMode = 5
  Placement = pos=(0,0,0) rot=(0.57735,0.57735,0.57735;2.0944rad)
  expr: Constraints[10] = VarSet.Tube_height / 2 - 20 mm
  expr: Constraints[8] = VarSet.Tube_width
  expr: Constraints[9] = VarSet.Tube_height / 2
  sketch-geometry (4):
    g0: LineSegment StartX=-25.25 StartY=30 StartZ=0 EndX=25.25 EndY=30 EndZ=0
    g1: LineSegment StartX=25.25 StartY=30 StartZ=0 EndX=25.25 EndY=50 EndZ=0
    g2: LineSegment StartX=25.25 StartY=50 StartZ=0 EndX=-25.25 EndY=50 EndZ=0
    g3: LineSegment StartX=-25.25 StartY=50 StartZ=0 EndX=-25.25 EndY=30 EndZ=0
  constraints (11):
    c: Coincident(g0,g1)
    c: Coincident(g1,g2)
    c: Coincident(g2,g3)
    c: Coincident(g3,g0)
    c: Horizontal(g0)
    c: Vertical(g1)
    c: Vertical(g3)
    c: Symmetric(g1,g2,g-2)
    c: Distance(g2) = 50.5
    c: DistanceY(g-1,g1) = 50
    c: DistanceY(g-1,g0) = 30
FEATURE [PartDesign::Pad] Pad017
  Direction = (1,0,0)
  Length = 15
  Length2 = 10
  Placement = pos=(0,0,0) rot=(1,1,1;2.0944rad)
  Profile = -> Sketch025
  ReferenceAxis = -> Sketch025 [N_Axis]
  Refine = true
  Suppressed = false
  Type = 0
FEATURE [PartDesign::Fillet] Fillet009
  Base = -> Pad017 [Edge8,Edge1,Edge2,Edge5]
  BaseFeature = -> Pad017
  Placement = pos=(0,0,0) rot=(1,1,1;2.0944rad)
  Radius = 8
  Refine = true
  SupportTransform = false
  Suppressed = false
  UseAllEdges = false
  expr: Radius = VarSet.Tube_fillet_radius
FEATURE [Sketcher::SketchObject] Sketch026
  ArcFitTolerance = 1e-06
  AttachmentSupport = -> [YZ_Plane017]
  ExternalGeometry = -> [Fillet009]
  FullyConstrained = true
  MakeInternals = false
  MapMode = 5
  Placement = pos=(0,0,0) rot=(0.57735,0.57735,0.57735;2.0944rad)
  expr: Constraints[7] = VarSet.Tube_thickness
  sketch-geometry (4):
    g0: LineSegment StartX=-17.15 StartY=46 StartZ=0 EndX=-17.15 EndY=30 EndZ=0
    g1: LineSegment StartX=-17.15 StartY=30 StartZ=0 EndX=17.15 EndY=30 EndZ=0
    g2: LineSegment StartX=17.15 StartY=30 StartZ=0 EndX=17.15 EndY=46 EndZ=0
    g3: LineSegment StartX=17.15 StartY=46 StartZ=0 EndX=-17.15 EndY=46 EndZ=0
  constraints (11):
    c: Coincident(g0,g1)
    c: Coincident(g1,g2)
    c: Coincident(g2,g3)
    c: Coincident(g3,g0)
    c: Vertical(g0)
    c: Vertical(g2)
    c: Horizontal(g1)
    c: Distance(g0,g-4) = 4
    c: PointOnObject(g0,g-3)
    c: Distance(g0,g-3) = 0.1
    c: Symmetric(g0,g2,g-2)
FEATURE [PartDesign::Pad] Pad018
  BaseFeature = -> Fillet009
  Direction = (1,0,0)
  Length = 15
  Length2 = 10
  Placement = pos=(0,0,0) rot=(1,1,1;2.0944rad)
  Profile = -> Sketch026
  ReferenceAxis = -> Sketch026 [N_Axis]
  Refine = true
  Reversed = true
  Suppressed = false
  Type = 0
FEATURE [PartDesign::Fillet] Fillet010
  Base = -> Pad018 [Edge32,Edge29,Edge30,Edge34]
  BaseFeature = -> Pad018
  Placement = pos=(0,0,0) rot=(1,1,1;2.0944rad)
  Radius = 2
  Refine = true
  SupportTransform = false
  Suppressed = false
  UseAllEdges = false
FEATURE [Sketcher::SketchObject] Sketch027
  ArcFitTolerance = 1e-06
  AttachmentSupport = -> [XY_Plane017]
  FullyConstrained = true
  MakeInternals = false
  MapMode = 5
  expr: Constraints[0] = VarSet.Tube_width / 2 - VarSet.Tube_fillet_radius - 1 mm
  expr: Constraints[1] = 4 / 2 + 1.5
  sketch-geometry (1):
    g0: Circle CenterX=3.5 CenterY=16.25 CenterZ=0 NormalX=0 NormalY=0 NormalZ=1 AngleXU=0 Radius=1.825
  constraints (3):
    c: DistanceY(g-1,g0) = 16.25
    c: DistanceX(g-2,g0) = 3.5
    c: Diameter(g0) = 3.65
FEATURE [PartDesign::Pocket] Pocket003
  BaseFeature = -> Fillet010
  Direction = (0,0,-1)
  Length = 5
  Length2 = 5
  Midplane = true
  Placement = pos=(0,0,0) rot=(1,1,1;2.0944rad)
  Profile = -> Sketch027
  ReferenceAxis = -> Sketch027 [N_Axis]
  Refine = true
  Suppressed = false
  Type = 1
FEATURE [Sketcher::SketchObject] Sketch028
  ArcFitTolerance = 1e-06
  AttachmentSupport = -> [XY_Plane017]
  FullyConstrained = true
  MakeInternals = false
  MapMode = 5
  sketch-geometry (1):
    g0: Circle CenterX=-5 CenterY=0 CenterZ=0 NormalX=0 NormalY=0 NormalZ=1 AngleXU=0 Radius=2.3
  constraints (3):
    c: PointOnObject(g0,g-1)
    c: DistanceX(g-2,g0) = -5
    c: Diameter(g0) = 4.6
FEATURE [PartDesign::Pocket] Pocket004
  BaseFeature = -> Pocket003
  Direction = (0,0,-1)
  Length = 5
  Length2 = 5
  Placement = pos=(0,0,0) rot=(1,1,1;2.0944rad)
  Profile = -> Sketch028
  ReferenceAxis = -> Sketch028 [N_Axis]
  Refine = true
  Reversed = true
  Suppressed = false
  Type = 1
FEATURE [Sketcher::SketchObject] Sketch029
  ArcFitTolerance = 1e-06
  AttachmentSupport = -> [Pocket004]
  FullyConstrained = false
  MakeInternals = false
  MapMode = 5
  Placement = pos=(15,0,0) rot=(0.57735,0.57735,0.57735;2.0944rad)
  expr: Constraints[2] = VarSet.Tube_height / 2 - 10 mm
  sketch-geometry (2):
    g0: Circle CenterX=-10 CenterY=40 CenterZ=0 NormalX=0 NormalY=0 NormalZ=1 AngleXU=0 Radius=5.4284
    g1: Circle CenterX=10 CenterY=40 CenterZ=0 NormalX=0 NormalY=0 NormalZ=1 AngleXU=0 Radius=4.43586
  constraints (3):
    c: Symmetric(g0,g1,g-2)
    c: Distance(g1,g0) = 20
    c: DistanceY(g-1,g0) = 40
FEATURE [PartDesign::Hole] Hole001
  BaseFeature = -> Pocket004
  CustomThreadClearance = 0
  Depth = 125.342
  DepthType = 1
  Diameter = 4.6
  DrillForDepth = false
  DrillPoint = 1
  DrillPointAngle = 118
  HoleCutCountersinkAngle = 90
  HoleCutCustomValues = false
  HoleCutDepth = 0
  HoleCutDiameter = 11
  HoleCutType = 2
  ModelThread = false
  Placement = pos=(0,0,0) rot=(1,1,1;2.0944rad)
  Profile = -> Sketch029
  Refine = true
  Suppressed = false
  Tapered = false
  TaperedAngle = 90
  ThreadClass = 0
  ThreadDepth = 125.342
  ThreadDepthType = 0
  ThreadDirection = 0
  ThreadFit = 0
  ThreadSize = 0
  ThreadType = 0
  Threaded = false
  UseCustomThreadClearance = false
FEATURE [PartDesign::Chamfer] Chamfer010
  Angle = 45
  Base = -> Hole001 [Edge53,Face20,Face19,Face17,Edge17]
  BaseFeature = -> Hole001
  ChamferType = 0
  FlipDirection = false
  Placement = pos=(0,0,0) rot=(1,1,1;2.0944rad)
  Refine = true
  Size = 0.8
  Size2 = 1
  SupportTransform = false
  Suppressed = false
  UseAllEdges = false
FEATURE [PartDesign::Body] Body013  label="Chain lock - non-adjustable"
  AllowCompound = false
  Group = -> [Sketch025,Pad017,Fillet009,Sketch026,Pad018,Fillet010,Sketch027,Pocket003,Sketch028,Pocket004,Sketch029,Hole001,Chamfer010]
  Origin = -> Origin017
  Placement = pos=(330,0,0) rot=(0,0,1;0rad)
  Tip = -> Chamfer010
  expr: .Placement.Base.x = Pad.Length / 2
COMPONENT P7 — recipe-attached ("Chain lock - adjustable", modeled in this document).
Construction recipe (the document's own serialized feature program — sketch geometry with constraints, then the solid features built on it; lengths are millimeters unless a unit is written):

FEATURE [Sketcher::SketchObject] Sketch030
  ArcFitTolerance = 1e-06
  AttachmentSupport = -> [YZ_Plane018]
  FullyConstrained = true
  MakeInternals = false
  MapMode = 5
  Placement = pos=(0,0,0) rot=(0.57735,0.57735,0.57735;2.0944rad)
  expr: Constraints[11] = VarSet.Tube_width
  expr: Constraints[13] = VarSet.Tube_width / 2 - VarSet.Tube_fillet_radius - 1 mm
  expr: Constraints[7] = VarSet.Tube_height / 2 - 20 mm
  expr: Constraints[8] = VarSet.Tube_height / 2 + 15 mm
  expr: Constraints[9] = VarSet.Tube_height / 2 + 25 mm
  sketch-geometry (5):
    g0: LineSegment StartX=-25.25 StartY=75 StartZ=0 EndX=-25.25 EndY=30 EndZ=0
    g1: LineSegment StartX=-25.25 StartY=30 StartZ=0 EndX=25.25 EndY=30 EndZ=0
    g2: LineSegment StartX=25.25 StartY=30 StartZ=0 EndX=25.25 EndY=75 EndZ=0
    g3: LineSegment StartX=25.25 StartY=75 StartZ=0 EndX=-25.25 EndY=75 EndZ=0
    g4: Circle CenterX=16.25 CenterY=65 CenterZ=0 NormalX=0 NormalY=0 NormalZ=1 AngleXU=0 Radius=1.825
  constraints (14):
    c: Coincident(g0,g1)
    c: Coincident(g1,g2)
    c: Coincident(g2,g3)
    c: Coincident(g3,g0)
    c: Vertical(g0)
    c: Vertical(g2)
    c: Horizontal(g3)
    c: DistanceY(g-1,g1) = 30
    c: DistanceY(g-1,g4) = 65
    c: DistanceY(g-1,g2) = 75
    c: Symmetric(g1,g0,g-2)
    c: Distance(g3) = 50.5
    c: Diameter(g4) = 3.65
    c: DistanceX(g-2,g4) = 16.25
FEATURE [PartDesign::Pad] Pad019
  Direction = (1,0,0)
  Length = 15
  Length2 = 10
  Placement = pos=(0,0,0) rot=(1,1,1;2.0944rad)
  Profile = -> Sketch030
  ReferenceAxis = -> Sketch030 [N_Axis]
  Refine = true
  Reversed = true
  Suppressed = false
  Type = 0
FEATURE [PartDesign::Fillet] Fillet011
  Base = -> Pad019 [Edge1,Edge2,Edge5,Edge8]
  BaseFeature = -> Pad019
  Placement = pos=(0,0,0) rot=(1,1,1;2.0944rad)
  Radius = 8
  Refine = true
  SupportTransform = false
  Suppressed = false
  UseAllEdges = false
  expr: Radius = VarSet.Tube_fillet_radius
FEATURE [Sketcher::SketchObject] Sketch031
  ArcFitTolerance = 1e-06
  AttachmentSupport = -> [Fillet011]
  ExternalGeometry = -> [Fillet011]
  FullyConstrained = true
  MakeInternals = false
  MapMode = 5
  Placement = pos=(0,0,0) rot=(0.57735,0.57735,0.57735;2.0944rad)
  expr: Constraints[10] = VarSet.Tube_height / 2 - VarSet.Tube_thickness
  sketch-geometry (4):
    g0: LineSegment StartX=-17.15 StartY=30 StartZ=0 EndX=17.15 EndY=30 EndZ=0
    g1: LineSegment StartX=17.15 StartY=30 StartZ=0 EndX=17.15 EndY=46 EndZ=0
    g2: LineSegment StartX=17.15 StartY=46 StartZ=0 EndX=-17.15 EndY=46 EndZ=0
    g3: LineSegment StartX=-17.15 StartY=46 StartZ=0 EndX=-17.15 EndY=30 EndZ=0
  constraints (11):
    c: Coincident(g0,g1)
    c: Coincident(g1,g2)
    c: Coincident(g2,g3)
    c: Coincident(g3,g0)
    c: Horizontal(g2)
    c: Vertical(g1)
    c: Vertical(g3)
    c: PointOnObject(g0,g-3)
    c: Symmetric(g0,g0,g-2)
    c: Distance(g0,g-3) = 0.1
    c: DistanceY(g-1,g1) = 46
FEATURE [PartDesign::Pad] Pad020
  BaseFeature = -> Fillet011
  Direction = (1,0,0)
  Length = 15
  Length2 = 10
  Placement = pos=(0,0,0) rot=(1,1,1;2.0944rad)
  Profile = -> Sketch031
  ReferenceAxis = -> Sketch031 [N_Axis]
  Refine = true
  Suppressed = false
  Type = 0
FEATURE [PartDesign::Fillet] Fillet012
  Base = -> Pad020 [Edge34,Edge36,Edge31,Edge32]
  BaseFeature = -> Pad020
  Placement = pos=(0,0,0) rot=(1,1,1;2.0944rad)
  Radius = 2
  Refine = true
  SupportTransform = false
  Suppressed = false
  UseAllEdges = false
FEATURE [Sketcher::SketchObject] Sketch032
  ArcFitTolerance = 1e-06
  AttachmentSupport = -> [Fillet012]
  FullyConstrained = false
  MakeInternals = false
  MapMode = 5
  Placement = pos=(0,1.65e-14,75) rot=(0,0,-1;1.5708rad)
  expr: Constraints[0] = -Pad019.Length / 2
  expr: Constraints[1] = -VarSet.Tube_width / 2 + VarSet.Tube_fillet_radius + 1 mm + 3.5 mm + 2.5 mm
  sketch-geometry (1):
    g0: Circle CenterX=-10.25 CenterY=-7.5 CenterZ=0 NormalX=0 NormalY=0 NormalZ=1 AngleXU=0 Radius=2.51289
  constraints (2):
    c: DistanceY(g-1,g0) = -7.5
    c: DistanceX(g-2,g0) = -10.25
FEATURE [PartDesign::Hole] Hole002
  BaseFeature = -> Fillet012
  CustomThreadClearance = 0
  Depth = 149.47
  DepthType = 1
  Diameter = 4.6
  DrillForDepth = false
  DrillPoint = 1
  DrillPointAngle = 118
  HoleCutCountersinkAngle = 90
  HoleCutCustomValues = false
  HoleCutDepth = 5
  HoleCutDiameter = 9.5
  HoleCutType = 1
  ModelThread = false
  Placement = pos=(0,0,0) rot=(1,1,1;2.0944rad)
  Profile = -> Sketch032
  Refine = true
  Suppressed = false
  Tapered = false
  TaperedAngle = 90
  ThreadClass = 0
  ThreadDepth = 149.47
  ThreadDepthType = 0
  ThreadDirection = 0
  ThreadFit = 0
  ThreadSize = 0
  ThreadType = 0
  Threaded = false
  UseCustomThreadClearance = false
FEATURE [Sketcher::SketchObject] Sketch033
  ArcFitTolerance = 1e-06
  AttachmentSupport = -> [Hole002]
  FullyConstrained = true
  MakeInternals = false
  MapMode = 5
  Placement = pos=(0,1.01e-14,46) rot=(0,0,-1;1.5708rad)
  sketch-geometry (1):
    g0: Circle CenterX=0 CenterY=7 CenterZ=0 NormalX=0 NormalY=0 NormalZ=1 AngleXU=0 Radius=2.3
  constraints (3):
    c: PointOnObject(g0,g-2)
    c: DistanceY(g-1,g0) = 7
    c: Diameter(g0) = 4.6
FEATURE [PartDesign::Pocket] Pocket005
  BaseFeature = -> Hole002
  Direction = (0,0,-1)
  Length = 5
  Length2 = 5
  Placement = pos=(0,0,0) rot=(1,1,1;2.0944rad)
  Profile = -> Sketch033
  ReferenceAxis = -> Sketch033 [N_Axis]
  Refine = true
  Suppressed = false
  Type = 1
FEATURE [Sketcher::SketchObject] Sketch034
  ArcFitTolerance = 1e-06
  AttachmentSupport = -> [Pocket005]
  FullyConstrained = true
  MakeInternals = false
  MapMode = 5
  Placement = pos=(-15,0,0) rot=(0.57735,0.57735,-0.57735;4.18879rad)
  expr: Constraints[2] = -VarSet.Tube_height / 2 + 10 mm
  sketch-geometry (2):
    g0: Circle CenterX=5.1 CenterY=-40 CenterZ=0 NormalX=0 NormalY=0 NormalZ=1 AngleXU=0 Radius=2.3
    g1: Circle CenterX=-9.9 CenterY=-40 CenterZ=0 NormalX=0 NormalY=0 NormalZ=1 AngleXU=0 Radius=2.3
  constraints (6):
    c: Equal(g0,g1)
    c: Diameter(g0) = 4.6
    c: DistanceY(g-1,g0) = -40
    c: Horizontal(g1,g0)
    c: DistanceX(g-2,g0) = 5.1
    c: Distance(g1,g0) = 15
FEATURE [PartDesign::Hole] Hole003
  BaseFeature = -> Pocket005
  CustomThreadClearance = 0
  Depth = 149.47
  DepthType = 1
  Diameter = 4.6
  DrillForDepth = false
  DrillPoint = 1
  DrillPointAngle = 118
  HoleCutCountersinkAngle = 90
  HoleCutCustomValues = false
  HoleCutDepth = 0
  HoleCutDiameter = 11
  HoleCutType = 2
  ModelThread = false
  Placement = pos=(0,0,0) rot=(1,1,1;2.0944rad)
  Profile = -> Sketch034
  Refine = true
  Suppressed = false
  Tapered = false
  TaperedAngle = 90
  ThreadClass = 0
  ThreadDepth = 149.47
  ThreadDepthType = 0
  ThreadDirection = 0
  ThreadFit = 0
  ThreadSize = 0
  ThreadType = 0
  Threaded = false
  UseCustomThreadClearance = false
FEATURE [PartDesign::Chamfer] Chamfer011
  Angle = 45
  Base = -> Hole003 [Edge49,Face18,Face20,Face21,Edge14,Face17]
  BaseFeature = -> Hole003
  ChamferType = 0
  FlipDirection = false
  Placement = pos=(0,0,0) rot=(1,1,1;2.0944rad)
  Refine = true
  Size = 0.8
  Size2 = 1
  SupportTransform = false
  Suppressed = false
  UseAllEdges = false
FEATURE [PartDesign::Body] Body014  label="Chain lock - adjustable"
  AllowCompound = false
  Group = -> [Sketch030,Pad019,Fillet011,Sketch031,Pad020,Fillet012,Sketch032,Hole002,Sketch033,Pocket005,Sketch034,Hole003,Chamfer011]
  Origin = -> Origin018
  Placement = pos=(-330,0,0) rot=(0,0,1;0rad)
  Tip = -> Chamfer011
  expr: .Placement.Base.x = -Pad.Length / 2
COMPONENT P8 — geometry summary ("Bicycle chain drive - positioned"; no construction recipe available for this part):
  bounding box: 660.0 x 141.5 x 109.0 mm
  tessellated surface: 82,862 triangles
  volume: 607996 mm^3 (6% of its bounding box)
COMPONENT P9 — recipe-attached ("Foot", modeled in this document).
Construction recipe (the document's own serialized feature program — sketch geometry with constraints, then the solid features built on it; lengths are millimeters unless a unit is written):

FEATURE [Sketcher::SketchObject] Sketch
  ArcFitTolerance = 1e-06
  AttachmentSupport = -> [YZ_Plane]
  FullyConstrained = true
  MakeInternals = false
  MapMode = 5
  Placement = pos=(0,0,0) rot=(0.57735,0.57735,0.57735;2.0944rad)
  expr: .Constraints.beamheight = VarSet.Tube_height
  expr: .Constraints.beamwidth = VarSet.Tube_width
  sketch-geometry (4):
    g0: LineSegment StartX=-25.25 StartY=-50 StartZ=0 EndX=25.25 EndY=-50 EndZ=0
    g1: LineSegment StartX=25.25 StartY=-50 StartZ=0 EndX=25.25 EndY=50 EndZ=0
    g2: LineSegment StartX=25.25 StartY=50 StartZ=0 EndX=-25.25 EndY=50 EndZ=0
    g3: LineSegment StartX=-25.25 StartY=50 StartZ=0 EndX=-25.25 EndY=-50 EndZ=0
  constraints (10):
    c: Horizontal(g2)
    c: Vertical(g3)
    c: Distance(g1,g3) = 50.5  'beamwidth'
    c: Distance(g0,g2) = 100  'beamheight'
    c: Coincident(g0,g1)
    c: Coincident(g2,g1)
    c: Coincident(g3,g0)
    c: Coincident(g2,g3)
    c: Symmetric(g0,g1,g-1)
    c: Symmetric(g0,g0,g-2)
FEATURE [PartDesign::Pad] Pad
  Direction = (1,0,0)
  Length = 660
  Length2 = 10
  Midplane = true
  Placement = pos=(0,0,0) rot=(1,1,1;2.0944rad)
  Profile = -> Sketch
  ReferenceAxis = -> Sketch [N_Axis]
  Refine = true
  Reversed = true
  Suppressed = false
  Type = 0
FEATURE [PartDesign::Fillet] Fillet
  Base = -> Pad [Edge5,Edge2,Edge8,Edge1]
  BaseFeature = -> Pad
  Placement = pos=(0,0,0) rot=(1,1,1;2.0944rad)
  Radius = 8
  Refine = true
  SupportTransform = false
  Suppressed = false
  UseAllEdges = false
  expr: Radius = VarSet.Tube_fillet_radius
FEATURE [PartDesign::Thickness] Thickness
  Base = -> Fillet [Face2,Face5]
  BaseFeature = -> Fillet
  Intersection = false
  Join = 0
  Mode = 0
  Refine = true
  Reversed = true
  SupportTransform = false
  Suppressed = false
  Value = 4
  expr: Value = VarSet.Tube_thickness
FEATURE [PartDesign::Body] Body  label="Steel tube"
  AllowCompound = false
  Group = -> [Sketch,Pad,Fillet,Thickness]
  Origin = -> Origin
  Tip = -> Thickness
COMPONENT P10 — same part as P9; its construction recipe is shown at P9.
COMPONENT P11 — recipe-attached ("Bearing ring 1", modeled in this document).
Construction recipe (the document's own serialized feature program — sketch geometry with constraints, then the solid features built on it; lengths are millimeters unless a unit is written):

FEATURE [Sketcher::SketchObject] Sketch003
  ArcFitTolerance = 1e-06
  AttachmentSupport = -> [YZ_Plane006]
  FullyConstrained = true
  MakeInternals = false
  MapMode = 5
  Placement = pos=(0,0,0) rot=(0.57735,0.57735,0.57735;2.0944rad)
  expr: .Constraints.y = VarSet.Tube_width / 2 + VarSet.Carriage_to_tube_clearance
  expr: .Constraints.z = VarSet.Tube_height / 2 + VarSet.Carriage_to_tube_clearance
  expr: Constraints[22] = VarSet.Tube_height / 2 + VarSet.Carriage_to_bearing_top_clearance + VarSet.Bearing_od
  expr: Constraints[23] = VarSet.Tube_width / 2 + VarSet.Carriage_to_bearing_top_clearance + VarSet.Bearing_od
  sketch-geometry (10):
    g0: LineSegment StartX=26.75 StartY=-51.5 StartZ=0 EndX=26.75 EndY=51.5 EndZ=0
    g1: LineSegment StartX=26.75 StartY=51.5 StartZ=0 EndX=-26.75 EndY=51.5 EndZ=0
    g2: LineSegment StartX=-26.75 StartY=51.5 StartZ=0 EndX=-26.75 EndY=-51.5 EndZ=0
    g3: LineSegment StartX=-26.75 StartY=-51.5 StartZ=0 EndX=26.75 EndY=-51.5 EndZ=0
    g4: GeomPoint [constr] X=0 Y=0 Z=0
    g5: LineSegment StartX=48.75 StartY=-73.5 StartZ=0 EndX=48.75 EndY=73.5 EndZ=0
    g6: LineSegment StartX=48.75 StartY=73.5 StartZ=0 EndX=-48.75 EndY=73.5 EndZ=0
    g7: LineSegment StartX=-48.75 StartY=73.5 StartZ=0 EndX=-48.75 EndY=-73.5 EndZ=0
    g8: LineSegment StartX=-48.75 StartY=-73.5 StartZ=0 EndX=48.75 EndY=-73.5 EndZ=0
    g9: GeomPoint [constr] X=0 Y=0 Z=0
  constraints (24):
    c: Coincident(g0,g1)
    c: Coincident(g1,g2)
    c: Coincident(g2,g3)
    c: Coincident(g3,g0)
    c: Vertical(g0)
    c: Vertical(g2)
    c: Horizontal(g1)
    c: Horizontal(g3)
    c: Symmetric(g2,g0,g4)
    c: Coincident(g4,g-1)
    c: Coincident(g5,g6)
    c: Coincident(g6,g7)
    c: Coincident(g7,g8)
    c: Coincident(g8,g5)
    c: Vertical(g5)
    c: Vertical(g7)
    c: Horizontal(g6)
    c: Horizontal(g8)
    c: Symmetric(g7,g5,g9)
    c: Coincident(g9,g4)
    c: DistanceY(g-1,g0) = 51.5  'z'
    c: DistanceX(g-2,g0) = 26.75  'y'
    c: DistanceY(g-1,g5) = 73.5
    c: DistanceX(g-2,g5) = 48.75
FEATURE [PartDesign::Pad] Pad002
  Direction = (1,0,0)
  Length = 48
  Length2 = 10
  Midplane = true
  Placement = pos=(0,0,0) rot=(1,1,1;2.0944rad)
  Profile = -> Sketch003
  ReferenceAxis = -> Sketch003 [N_Axis]
  Refine = true
  Suppressed = false
  Type = 0
  expr: Length = VarSet.Bearing_axle_screw_diameter + VarSet.Screw_offset + VarSet.Bearing_od + VarSet.Bearing_distance_from_edge * 2
FEATURE [Sketcher::SketchObject] Sketch006
  ArcFitTolerance = 1e-06
  AttachmentSupport = -> [YZ_Plane006]
  FullyConstrained = true
  MakeInternals = false
  MapMode = 5
  Placement = pos=(0,0,0) rot=(0.57735,0.57735,0.57735;2.0944rad)
  expr: Constraints[10] = Sketch003.Constraints.y - VarSet.Drive_chain_slot_width
  expr: Constraints[7] = Sketch003.Constraints.y
  expr: Constraints[8] = Sketch003.Constraints.z
  expr: Constraints[9] = VarSet.Tube_height / 2 + VarSet.Drive_chain_slot_height
  sketch-geometry (4):
    g0: LineSegment StartX=-1.75 StartY=51.5 StartZ=0 EndX=26.75 EndY=51.5 EndZ=0
    g1: LineSegment StartX=26.75 StartY=51.5 StartZ=0 EndX=26.75 EndY=60 EndZ=0
    g2: LineSegment StartX=26.75 StartY=60 StartZ=0 EndX=6.75 EndY=60 EndZ=0
    g3: LineSegment StartX=6.75 StartY=60 StartZ=0 EndX=-1.75 EndY=51.5 EndZ=0
  constraints (12):
    c: Coincident(g0,g1)
    c: Coincident(g1,g2)
    c: Coincident(g2,g3)
    c: Coincident(g3,g0)
    c: Horizontal(g0)
    c: Horizontal(g2)
    c: Vertical(g1)
    c: DistanceX(g-2,g0) = 26.75
    c: DistanceY(g-1,g0) = 51.5
    c: DistanceY(g-1,g1) = 60
    c: DistanceX(g-2,g2) = 6.75
    c: Angle(g-2,g3) = 2.35619
FEATURE [PartDesign::Pocket] Pocket
  BaseFeature = -> Pad002
  Direction = (-1,0,0)
  Length = 5
  Length2 = 5
  Midplane = true
  Placement = pos=(0,0,0) rot=(1,1,1;2.0944rad)
  Profile = -> Sketch006
  ReferenceAxis = -> Sketch006 [N_Axis]
  Refine = true
  Suppressed = false
  Type = 1
FEATURE [PartDesign::Fillet] Fillet006
  Base = -> Pocket [Edge26,Edge30,Edge29,Edge28]
  BaseFeature = -> Pocket
  Placement = pos=(0,0,0) rot=(1,1,1;2.0944rad)
  Radius = 9.5
  Refine = true
  SupportTransform = false
  Suppressed = false
  UseAllEdges = false
  expr: Radius = VarSet.Tube_fillet_radius + VarSet.Carriage_to_tube_clearance
FEATURE [PartDesign::Fillet] Fillet007
  Base = -> Fillet006 [Edge25,Edge29]
  BaseFeature = -> Fillet006
  Placement = pos=(0,0,0) rot=(1,1,1;2.0944rad)
  Radius = 2
  Refine = true
  SupportTransform = false
  Suppressed = false
  UseAllEdges = false
FEATURE [PartDesign::Chamfer] Chamfer
  Angle = 45
  Base = -> Fillet007 [Edge44,Edge46,Edge41]
  BaseFeature = -> Fillet007
  ChamferType = 0
  FlipDirection = false
  Placement = pos=(0,0,0) rot=(1,1,1;2.0944rad)
  Refine = true
  Size = 4
  Size2 = 1
  SupportTransform = false
  Suppressed = false
  UseAllEdges = false
FEATURE [Sketcher::SketchObject] Sketch021
  ArcFitTolerance = 1e-06
  AttachmentSupport = -> [YZ_Plane006]
  ExternalGeometry = -> [Chamfer]
  FullyConstrained = true
  MakeInternals = false
  MapMode = 5
  Placement = pos=(0,0,0) rot=(0.57735,0.57735,0.57735;2.0944rad)
  expr: Constraints[21] = VarSet.Bearing_axle_screw_diameter_loose_diamter
  sketch-geometry (14):
    g0: LineSegment StartX=48.75 StartY=73.5 StartZ=0 EndX=48.75 EndY=45.5 EndZ=0
    g1: LineSegment StartX=48.75 StartY=45.5 StartZ=0 EndX=57.75 EndY=54.5 EndZ=0
    g2: LineSegment StartX=57.75 StartY=54.5 StartZ=0 EndX=57.75 EndY=73.5 EndZ=0
    g3: LineSegment StartX=57.75 StartY=73.5 StartZ=0 EndX=48.75 EndY=73.5 EndZ=0
    g4: LineSegment StartX=19 StartY=73.5 StartZ=0 EndX=12 EndY=80.5 EndZ=0
    g5: LineSegment StartX=12 StartY=80.5 StartZ=0 EndX=2 EndY=80.5 EndZ=0
    g6: LineSegment StartX=19 StartY=73.5 StartZ=0 EndX=-5 EndY=73.5 EndZ=0
    g7: LineSegment StartX=-5 StartY=73.5 StartZ=0 EndX=2 EndY=80.5 EndZ=0
    g8: Circle [constr] CenterX=7 CenterY=72.5 CenterZ=0 NormalX=0 NormalY=0 NormalZ=1 AngleXU=0 Radius=4.25
    g9: Circle [constr] CenterX=49.75 CenterY=63.5 CenterZ=0 NormalX=0 NormalY=0 NormalZ=1 AngleXU=0 Radius=4.25
    g10: LineSegment [constr] StartX=49.75 StartY=63.5 StartZ=0 EndX=48.75 EndY=63.5 EndZ=0
    g11: LineSegment [constr] StartX=49.75 StartY=63.5 StartZ=0 EndX=49.75 EndY=73.5 EndZ=0
    g12: LineSegment [constr] StartX=7 StartY=72.5 StartZ=0 EndX=7 EndY=80.5 EndZ=0
    g13: LineSegment [constr] StartX=7 StartY=72.5 StartZ=0 EndX=7 EndY=73.5 EndZ=0
  constraints (44):
    c: Coincident(g0,g1)
    c: Coincident(g1,g2)
    c: Coincident(g2,g3)
    c: Coincident(g3,g0)
    c: Vertical(g0)
    c: Vertical(g2)
    c: Coincident(g0,g-3)
    c: Coincident(g4,g5)
    c: Horizontal(g5)
    c: Angle(g-3,g1) = 2.35619
    c: Angle(g-4,g3) = 3.14159
    c: Coincident(g4,g6)
    c: PointOnObject(g6,g-4)
    c: Horizontal(g6)
    c: Coincident(g6,g7)
    c: Coincident(g7,g5)
    c: Angle(g-4,g7) = 0.785398
    c: Angle(g4,g-4) = 0.785398
    c: Coincident(g10,g9)
    c: PointOnObject(g10,g0)
    c: Equal(g8,g9)
    c: Diameter(g8) = 8.5
    c: Angle(g-4,g10) = 3.14159
    c: Distance(g10) = 1
    c: Coincident(g11,g9)
    c: Angle(g-3,g11) = 3.14159
    c: PointOnObject(g11,g-4)
    c: Distance(g11) = 10
    c: DistanceX(g-2,g8) = 7
    c: Coincident(g12,g8)
    c: PointOnObject(g12,g5)
    c: Symmetric(g5,g4,g12)
    c: Distance(g12) = 8
    c: Distance(g5) = 10
    c: Distance(g3) = 9
    c: Distance(g0) = 28
    c: DistanceX(g-2,g8) = 7  'screw1y'
    c: DistanceY(g-1,g8) = 72.5  'screw1z'
    c: DistanceX(g-2,g9) = 49.75  'screw2y'
    c: DistanceY(g-1,g9) = 63.5  'screw2z'
    c: Coincident(g13,g8)
    c: Distance(g13) = 1
    c: Angle(g-2,g13) = 0
    c: PointOnObject(g13,g-4)
FEATURE [PartDesign::Pad] Pad015
  BaseFeature = -> Chamfer
  Direction = (1,0,0)
  Length = 48
  Length2 = 10
  Midplane = true
  Placement = pos=(0,0,0) rot=(1,1,1;2.0944rad)
  Profile = -> Sketch021
  ReferenceAxis = -> Sketch021 [N_Axis]
  Refine = true
  Suppressed = false
  Type = 0
  expr: Length = Pad002.Length
FEATURE [PartDesign::Chamfer] Chamfer007
  Angle = 45
  Base = -> Pad015 [Edge26]
  BaseFeature = -> Pad015
  ChamferType = 0
  FlipDirection = false
  Placement = pos=(0,0,0) rot=(1,1,1;2.0944rad)
  Refine = true
  Size = 4
  Size2 = 1
  SupportTransform = false
  Suppressed = false
  UseAllEdges = false
FEATURE [PartDesign::Fillet] Fillet008
  Base = -> Chamfer007 [Edge2,Edge3,Edge32,Edge30,Edge57,Edge58,Edge59,Edge60,Edge62,Edge64,Edge66,Edge65,Edge63,Edge61]
  BaseFeature = -> Chamfer007
  Placement = pos=(0,0,0) rot=(1,1,1;2.0944rad)
  Radius = 2
  Refine = true
  SupportTransform = false
  Suppressed = false
  UseAllEdges = false
FEATURE [Sketcher::SketchObject] Sketch022
  ArcFitTolerance = 1e-06
  AttachmentSupport = -> [YZ_Plane006]
  FullyConstrained = true
  MakeInternals = false
  MapMode = 5
  Placement = pos=(0,0,0) rot=(0.57735,0.57735,0.57735;2.0944rad)
  expr: .Constraints.holelocation = VarSet.Tube_width / 2 + VarSet.Bearing_od / 2
  expr: Constraints[0] = Sketch021.Constraints.screw1z
  expr: Constraints[1] = Sketch021.Constraints.screw1y
  expr: Constraints[2] = Sketch021.Constraints.screw2z
  expr: Constraints[3] = Sketch021.Constraints.screw2y
  expr: Constraints[9] = VarSet.Bearing_axle_screw_diameter_loose_diamter
  sketch-geometry (6):
    g0: Circle CenterX=7 CenterY=72.5 CenterZ=0 NormalX=0 NormalY=0 NormalZ=1 AngleXU=0 Radius=4.25
    g1: Circle CenterX=49.75 CenterY=63.5 CenterZ=0 NormalX=0 NormalY=0 NormalZ=1 AngleXU=0 Radius=4.25
    g2: Circle CenterX=36.25 CenterY=15 CenterZ=0 NormalX=0 NormalY=0 NormalZ=1 AngleXU=0 Radius=4.25
    g3: Circle CenterX=36.25 CenterY=-15 CenterZ=0 NormalX=0 NormalY=0 NormalZ=1 AngleXU=0 Radius=4.25
    g4: Circle CenterX=-36.25 CenterY=-15 CenterZ=0 NormalX=0 NormalY=0 NormalZ=1 AngleXU=0 Radius=4.25
    g5: Circle CenterX=-36.25 CenterY=15 CenterZ=0 NormalX=0 NormalY=0 NormalZ=1 AngleXU=0 Radius=4.25
  constraints (15):
    c: DistanceY(g-1,g0) = 72.5
    c: DistanceX(g-2,g0) = 7
    c: DistanceY(g-1,g1) = 63.5
    c: DistanceX(g-2,g1) = 49.75
    c: Equal(g5,g4)
    c: Equal(g5,g2)
    c: Equal(g5,g3)
    c: Equal(g5,g1)
    c: Equal(g5,g0)
    c: Diameter(g5) = 8.5
    c: Symmetric(g4,g5,g-1)
    c: Symmetric(g3,g2,g-1)
    c: Symmetric(g2,g5,g-2)
    c: Distance(g3,g2) = 30  'holespacing'
    c: DistanceX(g-2,g3) = 36.25  'holelocation'
FEATURE [PartDesign::Pocket] Pocket002
  BaseFeature = -> Fillet008
  Direction = (-1,0,0)
  Length = 5
  Length2 = 5
  Midplane = true
  Placement = pos=(0,0,0) rot=(1,1,1;2.0944rad)
  Profile = -> Sketch022
  ReferenceAxis = -> Sketch022 [N_Axis]
  Refine = true
  Suppressed = false
  Type = 1
FEATURE [PartDesign::Chamfer] Chamfer008
  Angle = 45
  Base = -> Pocket002 [Face5,Face2]
  BaseFeature = -> Pocket002
  ChamferType = 0
  FlipDirection = false
  Placement = pos=(0,0,0) rot=(1,1,1;2.0944rad)
  Refine = true
  Size = 0.6
  Size2 = 1
  SupportTransform = false
  Suppressed = false
  UseAllEdges = false
FEATURE [PartDesign::Body] Body002  label="Carriage body"
  AllowCompound = false
  Group = -> [Sketch003,Pad002,Sketch006,Pocket,Fillet006,Fillet007,Chamfer,Sketch021,Pad015,Chamfer007,Fillet008,Sketch022,Pocket002,Chamfer008]
  Origin = -> Origin006
  Tip = -> Chamfer008
PROVENANCE & LICENSES
A FreeCAD (.FCStd) document from a public repository crawl; recipes are the document's own serialized feature recipes (and, for linked parts, companion documents' recipes).
License: as declared in the source repository (recorded in the dataset sidecar).
